# Revit family: BVN_EA
name_source: partatom
category: Mechanical Equipment
units: mm (PartAtom-declared; Revit-internal decimal feet)

## family parameters
Always vertical = Yes
Cut with Voids When Loaded = No
Host = Wall
Part Type = Normal
Room Calculation Point = No
Round Connector Dimension = Use Diameter
Shared = No

## types (3) — shared parameters
Current = 0 A
Description = Plastic Fan
Frequency = 50 Hz
Insulation Thickness = B
Manufacturer = http://www.bahcivanmotor.com.tr
Material Fan = <By Category>
Model = EF
Protection Class = 20
URL = http://www.bahcivanmotor.com.tr
Voltage = 230 V

## per-type parameters (varying)
| type | A | Air Flow | B | C | D | D' | E | Material Cover | Menfez | Power | Q | Q' | Sound Pressure | Speed(d/d) | Weight | b |
| EA 1010 | 149 mm  [stored 0.488845 ft] | 100.00 m³/h | 35 mm  [stored 0.114829 ft] | 54 mm  [stored 0.177165 ft] | 97 mm  [stored 0.318241 ft] | 137 mm | 149 mm  [stored 0.488845 ft] | Stainless Steel | 119 mm  [stored 0.39042 ft] | 13 W | 75 mm  [stored 0.246063 ft] | 45 mm  [stored 0.147638 ft] | 40 | 2600 | 0.52 kg | 26 mm |
| EA 1219 | 188 mm  [stored 0.616798 ft] | 200.00 m³/h | 38 mm  [stored 0.124672 ft] | 76 mm  [stored 0.249344 ft] | 118 mm | 158 mm | 188 mm  [stored 0.616798 ft] | Default | 158 mm | 14 W | 94 mm  [stored 0.308399 ft] | 64 mm  [stored 0.209974 ft] | 41 | 2400 | 0.60 kg | 29 mm |
| EA 1530 | 208 mm | 300.00 m³/h | 45 mm  [stored 0.147638 ft] | 73 mm  [stored 0.239501 ft] | 149 mm  [stored 0.488845 ft] | 189 mm  [stored 0.620079 ft] | 208 mm | Default | 178 mm  [stored 0.58399 ft] | 21 W | 104 mm  [stored 0.341207 ft] | 74 mm | 43 | 2000 | 1.12 kg | 34 mm |

note: [stored X ft] marks values corroborated as IEEE doubles in the binary element streams (Revit-internal decimal feet)

## geometry (parser evidence)
native form markers: Sweep x2
no freeform markers — native parametric forms only
